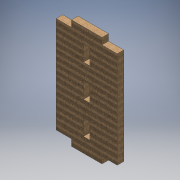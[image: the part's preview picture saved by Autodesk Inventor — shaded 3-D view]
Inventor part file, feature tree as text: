
AUTODESK INVENTOR PART (.ipt)
format: ipt  version: 2016 (Build 200138000, 138)  size: 167,936 bytes
history: native  units: mm
features: extrude x1, sketch x1
ambient origin geometry x8: Origin, YZ Plane, XZ Plane, XY Plane, X Axis, Y Axis, Z Axis, Center Point
bodies: Body1 (feature_tree)
feature tree (2):
  extrude  "Extrusion4"  Depth=14.945mm
  sketch  "Sketch1"  dims[d0=29.89mm d1=14.945mm d2=14.945mm d3=6.39mm d4=15.766857mm d6=6.3261mm d7=94.601145mm d15=7.883429mm d45=30.0mm d47=31.533715mm d48=10.0mm d50=10.0mm d52=6.39mm d53=0.0mm]
